# Revit family: ONUA
name_source: partatom
category: Mechanical Equipment
units: mm (PartAtom-declared; Revit-internal decimal feet)

## family parameters
Always vertical = Yes
Cut with Voids When Loaded = No
OmniClass Number = 23.40.40.11.17
OmniClass Title = Refrigerated Cases
Part Type = Normal
Room Calculation Point = No
Round Connector Dimension = Use Radius
Shared = No
Work Plane-Based = Yes

## types (2) — shared parameters
ANTI SWEAT APPARENT LOAD = 0 VA
ANTI SWEAT HEATER AMPS = 0 A
ANTI SWEAT HEATER WATTAGE = 0 W
BASE HEIGHT = 11"
BTU PER FOOT CONVENTIONAL = 1548
BTU PER FOOT PARALLEL = 1322
CERTIFICATIONS = NSF 7, UL471, CSA
COIL REFRIGERATION CHARGE = 0.00 lb
CONTROL TYPE = T-STAT
DATE = 02/06/12
DEDICATED CIRCUIT = YES
DEFROST PHASE = 1
DEFROST TIME AND DURATION = 2 @ 60 MIN
DEFROST WATTAGE = 0 W
DIEBOARD HEIGHT = 0"
DISCHARGE AIR TEMPERATURE = 31 °F
DRAIN LINE CONNECTION = Drain Connection
DRAIN LINE DIAMETER = 2"
DRAIN LINE RADIUS = 1"
DRAIN PIPE LENGTH = 0"
DRAIN PIPE TYPE = PVC
DRIP PAN PLUMB TYPE = HARD
Default Elevation = 48"
Description = MULTI DECK MERCHANDISER
ELECTRIC DEFROST = No
ELECTRICAL DEFROST VOLTAGE = 0 V
EVAPORATOR TEMPERATURE = 17 °F
FAN CONNECTOR DESCRIPTION = FAN AND ANTI SWEAT CONNECTOR
FAN NUMBER OF POLES = 1
FAN TYPE = ECM
GROUND FAULT PROTECTION = NO
HEIGHT = 87 5/16"
HOT GAS DEFROST = No
ISOLATED GROUND REQUIRED = NO
Keynote = DAIRY/DELI/MEAT/PRODUCE
LED LIGHTING AMPS = 0 A
LED LIGHTING AMPS PER ROW = 0 A
LIGHT TYPE = T8 FLUORESCENT
LIGHTING CONNECTION DESCRIPTION = LIGHTING CONNECTOR
LIGHTING NUMBER OF POLES = 1
LIQUID LINE CONNECTION = LIQUID LINE CONNECTION
LIQUID LINE DIAMETER = 0"
LIQUID LINE RADIUS = 0"
Manufacturer = HILL PHOENIX
NUMBER OF WIRES = 3
PHASE = 1
POWER FACTOR = 1
PRESSURE REGULATOR = 0.00 psi
RECEPTICAL MOUNTING HEIGHT ABOVE FLOOR = 19 3/4"
REF PIPE LENGTH = 28 5/8"
REF PLANE FRONT BACK = 17 15/16"
REVERSE AIR DEFROST = No
SET BACK MODE FOR ENERGY CONSERVATION = NO
SHELVE 1 = Yes
SHELVE 2 = No
SIZE OF COLD WATER HOOK UP = 0"
SIZE OF HOT WATER HOOK-UP = 0"
SUCTION LINE CONNECTION = SUCTION LINE CONNECTION
SUCTION LINE DIAMETER = 1"
SUCTION LINE RADIUS = 0"
T8 LIGHT OR LED LIGHT = Yes
T8 LIGHTING AMPS PER ROW = 0 A
TIME OFF DEFROST = Yes
TOEKICK HEIGHT = 5 1/2"
TOEKICK INSET = 1 1/2"
TOTAL CASE AMPS = 1 A
URL = http://www.hillphoenix.com
VOLTAGE = 120 V
WATER LINE MOUNTING HEIGHT ABOVE FLOOR = 0"
WEIGHT = 0.00 lb
WIDTH = 35 13/16"
zero-valued in all types: CORNICE AND NOSE LIGHT ROWS

## per-type parameters (varying)
- ONUA-6'/71"-5"BF: BTU ADD FOR LIGHTS=720; BTU ADD PER SHELF PER FOOT=60; CONVENTIONAL EVAPORATOR LOAD=10008; DEFROST AMPS=3 A; FAN AMPS=1 A; FAN AND ANTI SWEAT HEATER APPARENT LOAD=84 VA; FAN APPARENT LOAD=84 VA; FAN QUANTITY=3; FAN WATTAGE=42 W; LED LIGHTING BTU ADD PER ROW=27; LED LIGHTING WATTAGE=34 W; LEGEND NUMBER=ONU-6'/71"; LENGTH=72"; LENGTH FOR BTU=6; LIGHT AMPS=1 A; LIGHTING APPARENT LOAD=89 VA; LIGHTING WATTAGE=89 VA; Model=ONU-6'/71"; PARALLEL EVAPORATOR LOAD=8652; REF PLANE LEFT RIGHT=36"; SHELF LIGHT ROWS=2; SHELVE 3=Yes; SHELVE LENGTH=36"; T8 LIGHTING AMPS=1 A; T8 LIGHTING BTU ADD PER ROW=60; T8 LIGHTING WATTAGE=89 W; TOTAL APPARENT FAN-LIGHT AND A/S LOAD=131 VA; TOTAL CASE WATTAGE=131 W
- ONUA-4'/47"-5"BF: BTU ADD FOR LIGHTS=320; BTU ADD PER SHELF PER FOOT=80; CONVENTIONAL EVAPORATOR LOAD=6512; DEFROST AMPS=2 A; FAN AMPS=0 A; FAN AND ANTI SWEAT HEATER APPARENT LOAD=56 VA; FAN APPARENT LOAD=56 VA; FAN QUANTITY=2; FAN WATTAGE=28 W; LED LIGHTING BTU ADD PER ROW=36; LED LIGHTING WATTAGE=12 W; LEGEND NUMBER=ONU-4'/47"; LENGTH=48"; LENGTH FOR BTU=4; LIGHT AMPS=0 A; LIGHTING APPARENT LOAD=28 VA; LIGHTING WATTAGE=28 VA; Model=ONU-4'/47"; PARALLEL EVAPORATOR LOAD=5608; REF PLANE LEFT RIGHT=24"; SHELF LIGHT ROWS=1; SHELVE 3=No; SHELVE LENGTH=48"; T8 LIGHTING AMPS=0 A; T8 LIGHTING BTU ADD PER ROW=80; T8 LIGHTING WATTAGE=28 W; TOTAL APPARENT FAN-LIGHT AND A/S LOAD=56 VA; TOTAL CASE WATTAGE=56 W

## geometry (parser evidence)
native form markers: Blend x2, Sweep x3
no freeform markers — native parametric forms only
